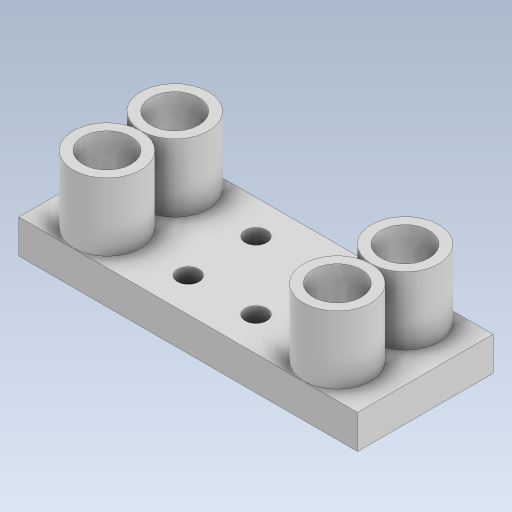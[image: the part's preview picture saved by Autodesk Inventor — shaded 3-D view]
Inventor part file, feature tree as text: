
AUTODESK INVENTOR PART (.ipt)
format: ipt  version: 2023.5 (Build 275446000, 446)  size: 376,320 bytes
history: native  units: mm
features: extrude x2, sketch x1
ambient origin geometry x8: Origin, YZ Plane, XZ Plane, XY Plane, X Axis, Y Axis, Z Axis, Center Point
bodies: Solid1 (feature_tree)
feature tree (3):
  sketch  "Sketch1"  dims[d0=50.0mm d1=20.0mm d2=7.1mm d3=5.0mm d4=3.2mm d5=12.0mm d6=10.0mm d7=10.0mm d8=10.0mm d9=10.0mm d10=5.0mm d11=0.0mm d12=15.0mm d13=0.0mm]
  extrude  "Extrusion1"  Depth=20.0mm
  extrude  "Extrusion2"  Depth=15.0mm
